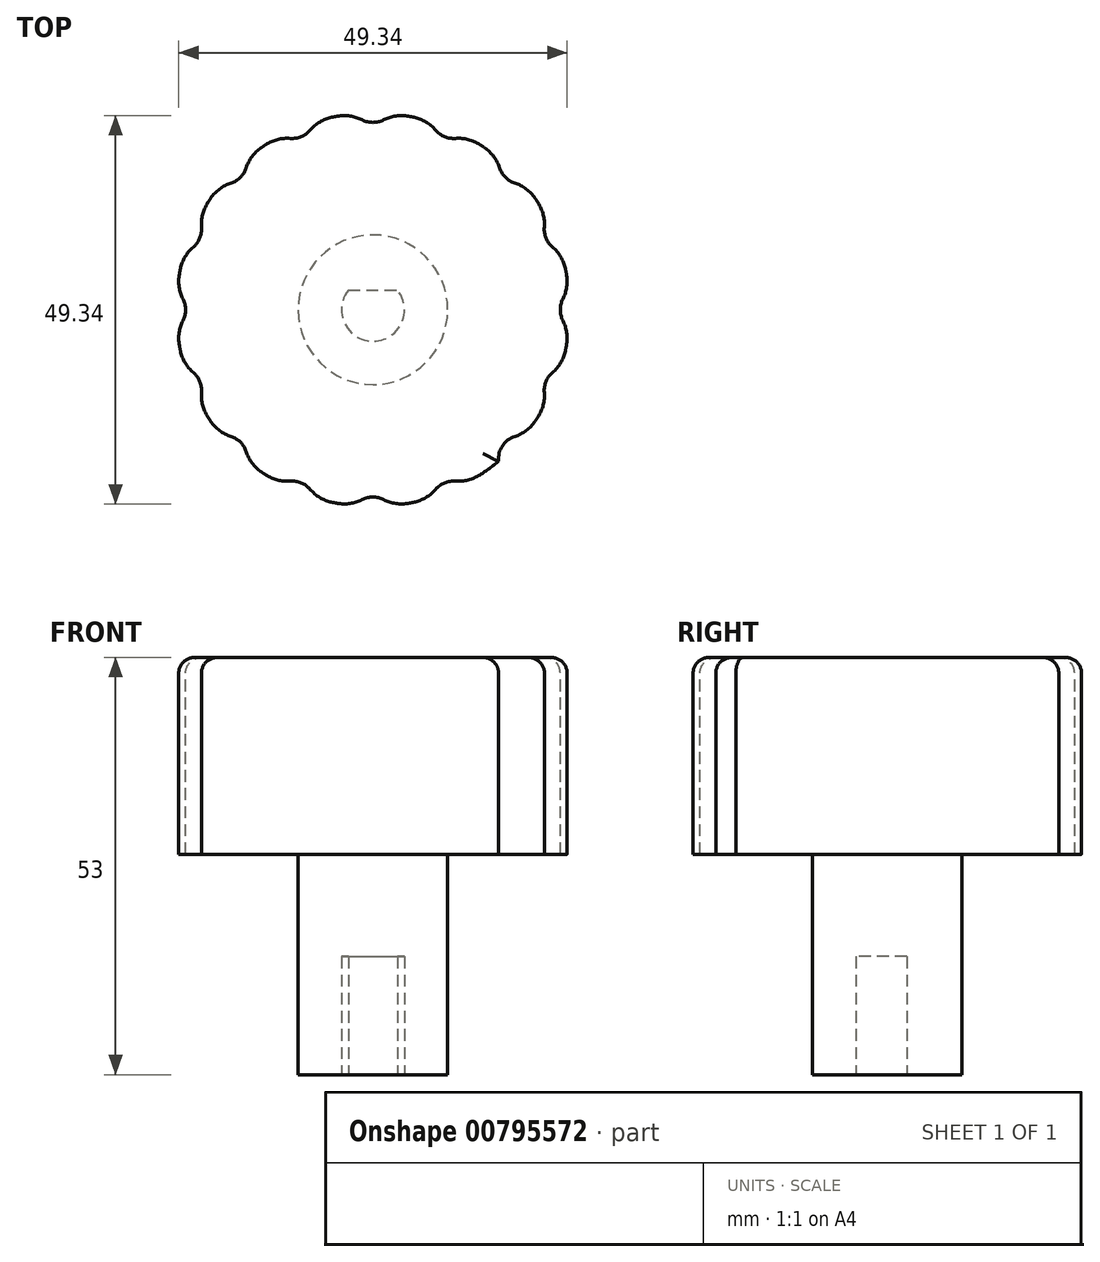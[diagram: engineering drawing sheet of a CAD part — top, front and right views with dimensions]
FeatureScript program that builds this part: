
annotation { "Feature Type Name" : "Feature", "Feature Type Description" : "" }
export const myFeature = defineFeature(function(context is Context, id is Id, definition is map)
    precondition{}
    {
        {
            var Q0;
            Q0=qCreatedBy(makeId("Top.planeOp"),FACE);
            cPlane(context, id + "F0", {"entities" : qUnion([Q0]), "cplaneType" : CPlaneType.OFFSET, "offset" : 25 * mm, "oppositeDirection" : true, "width" : 152.4 * mm, "height" : 152.4 * mm});
        }
        {
            var Q0;
            Q0=qCreatedBy(id+"F0.planeOp",FACE);
            cPlane(context, id + "F1", {"entities" : qUnion([Q0]), "cplaneType" : CPlaneType.OFFSET, "offset" : 1 * mm, "oppositeDirection" : true, "width" : 150 * mm, "height" : 150 * mm});
        }
        {
            var Q0;
            Q0=qCreatedBy(id+"F1.planeOp",FACE);
            cPlane(context, id + "F2", {"entities" : qUnion([Q0]), "cplaneType" : CPlaneType.OFFSET, "offset" : 27 * mm, "oppositeDirection" : true, "width" : 150 * mm, "height" : 150 * mm});
        }
        {
            var Q0;
            Q0=qCreatedBy(makeId("Top.planeOp"),FACE);
            var sketch = newSketch(context, id + "F3", { "sketchPlane" : qUnion([Q0])});
            skCircle(sketch, "E0", {"center": v(0, 0) * mm, "radius": 25 * mm});
            skSolve(sketch);
        }
        {
            var Q0;
            Q0=makeQuery(id+"F3.imprint","IMPRINT",FACE,{"disambiguationData":[TD([[makeQuery(id+"F3.imprint","IMPRINT",EDGE,{"derivedFrom":sQuery(id+"F3.wireOp",EDGE,"E0")}),1.0]])]});
            var Q1;
            Q1=qCreatedBy(id+"F0.planeOp",FACE);
            extrude(context, id + "F4", {"entities" : qUnion([Q0]), "endBound" : BoundingType.UP_TO_SURFACE, "oppositeDirection" : true, "depth" : 25 * mm, "endBoundEntityFace" : qUnion([Q1]), "offsetDistance" : 25 * mm});
        }
        {
            var Q0;
            Q0=qCreatedBy(id+"F0.planeOp",FACE);
            var sketch = newSketch(context, id + "F5", { "sketchPlane" : qUnion([Q0])});
            skCircle(sketch, "E1", {"center": v(0, 0) * mm, "radius": 9.5 * mm});
            skSolve(sketch);
        }
        {
            var Q0;
            Q0 = qSketchRegion(id + "F5", true);
            var Q1;
            Q1=qCreatedBy(id+"F2.planeOp",FACE);
            extrude(context, id + "F6", {"entities" : qUnion([Q0]), "operationType" : NewBodyOperationType.ADD, "endBound" : BoundingType.UP_TO_SURFACE, "oppositeDirection" : true, "depth" : 25 * mm, "endBoundEntityFace" : qUnion([Q1]), "offsetDistance" : 25 * mm});
        }
        {
            var Q0;
            Q0=qCreatedBy(id+"F2.planeOp",FACE);
            var sketch = newSketch(context, id + "F7", { "sketchPlane" : qUnion([Q0])});
            skArc(sketch, "E2", {"start": v(-3.12, 2.5) * mm, "mid": v(0, -4) * mm, "end": v(3.12, 2.5) * mm});
            skLineSegment(sketch, "E3", {"start": v(-3.12, 2.5) * mm, "end": v(3.12, 2.5) * mm});
            skSolve(sketch);
        }
        {
            var Q0;
            Q0=makeQuery(id+"F7.imprint","IMPRINT",FACE,{"disambiguationData":[TD([[makeQuery(id+"F7.imprint","IMPRINT",EDGE,{"derivedFrom":sQuery(id+"F7.wireOp",EDGE,"E2")}),1.0]])]});
            extrude(context, id + "F8", {"entities" : qUnion([Q0]), "operationType" : NewBodyOperationType.REMOVE, "depth" : 15 * mm, "offsetDistance" : 25 * mm});
        }
        {
            var Q0;
            Q0=qCreatedBy(makeId("Top.planeOp"),FACE);
            var sketch = newSketch(context, id + "F9", { "sketchPlane" : qUnion([Q0])});
            skCircle(sketch, "E4", {"center": v(0, 26.8) * mm, "radius": 3 * mm});
            skSolve(sketch);
        }
        {
            var Q0;
            Q0=makeQuery(id+"F9.imprint","IMPRINT",FACE,{"disambiguationData":[TD([[makeQuery(id+"F9.imprint","IMPRINT",EDGE,{"derivedFrom":sQuery(id+"F9.wireOp",EDGE,"E4")}),1.0]])]});
            var Q1;
            Q1=makeQuery(id+"F4.opExtrude","CAP_FACE",FACE,{"disambiguationData":[OSD([sQuery(id+"F3.wireOp",EDGE,"E0")])],"isStart":false});
            extrude(context, id + "F10", {"entities" : qUnion([Q0]), "endBound" : BoundingType.UP_TO_SURFACE, "oppositeDirection" : true, "depth" : 25 * mm, "endBoundEntityFace" : qUnion([Q1]), "offsetDistance" : 25 * mm});
        }
        {
            var Q0;
            Q0=makeQuery(id+"F10.opExtrude","SWEPT_BODY",BODY,{"disambiguationData":[OSD([sQuery(id+"F9.wireOp",EDGE,"E4")])]});
            var Q1;
            Q1=makeQuery(id+"F4.opExtrude","CAP_EDGE",EDGE,{"disambiguationData":[OSD([sQuery(id+"F3.wireOp",EDGE,"E0")])],"isStart":true});
            circularPattern(context, id + "F11", {"entities" : qUnion([Q0]), "axis" : qUnion([Q1]), "angle" : 360 * degree, "instanceCount" : 16, "equalSpace" : true});
        }
        {
            var Q0;
            Q0=makeQuery(id+"F10.opExtrude","SWEPT_BODY",BODY,{"disambiguationData":[OSD([sQuery(id+"F9.wireOp",EDGE,"E4")])]});
            var Q1;
            Q1=makeQuery(id+"F11.opPattern","COPY",BODY,{"derivedFrom":makeQuery(id+"F10.opExtrude","SWEPT_BODY",BODY,{"disambiguationData":[OSD([sQuery(id+"F9.wireOp",EDGE,"E4")])]}),"instanceName":"1"});
            var Q2;
            Q2=makeQuery(id+"F11.opPattern","COPY",BODY,{"derivedFrom":makeQuery(id+"F10.opExtrude","SWEPT_BODY",BODY,{"disambiguationData":[OSD([sQuery(id+"F9.wireOp",EDGE,"E4")])]}),"instanceName":"2"});
            var Q3;
            Q3=makeQuery(id+"F11.opPattern","COPY",BODY,{"derivedFrom":makeQuery(id+"F10.opExtrude","SWEPT_BODY",BODY,{"disambiguationData":[OSD([sQuery(id+"F9.wireOp",EDGE,"E4")])]}),"instanceName":"3"});
            var Q4;
            Q4=makeQuery(id+"F11.opPattern","COPY",BODY,{"derivedFrom":makeQuery(id+"F10.opExtrude","SWEPT_BODY",BODY,{"disambiguationData":[OSD([sQuery(id+"F9.wireOp",EDGE,"E4")])]}),"instanceName":"4"});
            var Q5;
            Q5=makeQuery(id+"F11.opPattern","COPY",BODY,{"derivedFrom":makeQuery(id+"F10.opExtrude","SWEPT_BODY",BODY,{"disambiguationData":[OSD([sQuery(id+"F9.wireOp",EDGE,"E4")])]}),"instanceName":"5"});
            var Q6;
            Q6=makeQuery(id+"F11.opPattern","COPY",BODY,{"derivedFrom":makeQuery(id+"F10.opExtrude","SWEPT_BODY",BODY,{"disambiguationData":[OSD([sQuery(id+"F9.wireOp",EDGE,"E4")])]}),"instanceName":"6"});
            var Q7;
            Q7=makeQuery(id+"F11.opPattern","COPY",BODY,{"derivedFrom":makeQuery(id+"F10.opExtrude","SWEPT_BODY",BODY,{"disambiguationData":[OSD([sQuery(id+"F9.wireOp",EDGE,"E4")])]}),"instanceName":"7"});
            var Q8;
            Q8=makeQuery(id+"F11.opPattern","COPY",BODY,{"derivedFrom":makeQuery(id+"F10.opExtrude","SWEPT_BODY",BODY,{"disambiguationData":[OSD([sQuery(id+"F9.wireOp",EDGE,"E4")])]}),"instanceName":"8"});
            var Q9;
            Q9=makeQuery(id+"F11.opPattern","COPY",BODY,{"derivedFrom":makeQuery(id+"F10.opExtrude","SWEPT_BODY",BODY,{"disambiguationData":[OSD([sQuery(id+"F9.wireOp",EDGE,"E4")])]}),"instanceName":"9"});
            var Q10;
            Q10=makeQuery(id+"F11.opPattern","COPY",BODY,{"derivedFrom":makeQuery(id+"F10.opExtrude","SWEPT_BODY",BODY,{"disambiguationData":[OSD([sQuery(id+"F9.wireOp",EDGE,"E4")])]}),"instanceName":"10"});
            var Q11;
            Q11=makeQuery(id+"F11.opPattern","COPY",BODY,{"derivedFrom":makeQuery(id+"F10.opExtrude","SWEPT_BODY",BODY,{"disambiguationData":[OSD([sQuery(id+"F9.wireOp",EDGE,"E4")])]}),"instanceName":"11"});
            var Q12;
            Q12=makeQuery(id+"F11.opPattern","COPY",BODY,{"derivedFrom":makeQuery(id+"F10.opExtrude","SWEPT_BODY",BODY,{"disambiguationData":[OSD([sQuery(id+"F9.wireOp",EDGE,"E4")])]}),"instanceName":"12"});
            var Q13;
            Q13=makeQuery(id+"F11.opPattern","COPY",BODY,{"derivedFrom":makeQuery(id+"F10.opExtrude","SWEPT_BODY",BODY,{"disambiguationData":[OSD([sQuery(id+"F9.wireOp",EDGE,"E4")])]}),"instanceName":"13"});
            var Q14;
            Q14=makeQuery(id+"F11.opPattern","COPY",BODY,{"derivedFrom":makeQuery(id+"F10.opExtrude","SWEPT_BODY",BODY,{"disambiguationData":[OSD([sQuery(id+"F9.wireOp",EDGE,"E4")])]}),"instanceName":"14"});
            var Q15;
            Q15=makeQuery(id+"F11.opPattern","COPY",BODY,{"derivedFrom":makeQuery(id+"F10.opExtrude","SWEPT_BODY",BODY,{"disambiguationData":[OSD([sQuery(id+"F9.wireOp",EDGE,"E4")])]}),"instanceName":"15"});
            var Q16;
            Q16=makeQuery(id+"F4.opExtrude","SWEPT_BODY",BODY,{"disambiguationData":[OSD([sQuery(id+"F3.wireOp",EDGE,"E0")])]});
            booleanBodies(context, id + "F12", {"operationType" : BooleanOperationType.SUBTRACTION, "tools" : qUnion([Q0, Q1, Q2, Q3, Q4, Q5, Q6, Q7, Q8, Q9, Q10, Q11, Q12, Q13, Q14, Q15]), "targets" : qUnion([Q16])});
        }
        {
            var Q0;
            Q0=makeQuery(id+"F12.opBoolean","INTERSECT",EDGE,{"disambiguationData":[OD(0.0)],"derivedFrom":[makeQuery(id+"F4.opExtrude","SWEPT_FACE",FACE,{"disambiguationData":[OSD([sQuery(id+"F3.wireOp",EDGE,"E0")])]}),makeQuery(id+"F10.opExtrude","SWEPT_FACE",FACE,{"disambiguationData":[OSD([sQuery(id+"F9.wireOp",EDGE,"E4")])]})]});
            var Q1;
            Q1=makeQuery(id+"F12.opBoolean","INTERSECT",EDGE,{"disambiguationData":[OD(1.0)],"derivedFrom":[makeQuery(id+"F4.opExtrude","SWEPT_FACE",FACE,{"disambiguationData":[OSD([sQuery(id+"F3.wireOp",EDGE,"E0")])]}),makeQuery(id+"F10.opExtrude","SWEPT_FACE",FACE,{"disambiguationData":[OSD([sQuery(id+"F9.wireOp",EDGE,"E4")])]})]});
            var Q2;
            Q2=makeQuery(id+"F12.opBoolean","INTERSECT",EDGE,{"disambiguationData":[OD(0.0)],"derivedFrom":[makeQuery(id+"F4.opExtrude","SWEPT_FACE",FACE,{"disambiguationData":[OSD([sQuery(id+"F3.wireOp",EDGE,"E0")])]}),makeQuery(id+"F11.opPattern","COPY",FACE,{"derivedFrom":makeQuery(id+"F10.opExtrude","SWEPT_FACE",FACE,{"disambiguationData":[OSD([sQuery(id+"F9.wireOp",EDGE,"E4")])]}),"instanceName":"15"})]});
            var Q3;
            Q3=makeQuery(id+"F12.opBoolean","INTERSECT",EDGE,{"disambiguationData":[OD(1.0)],"derivedFrom":[makeQuery(id+"F4.opExtrude","SWEPT_FACE",FACE,{"disambiguationData":[OSD([sQuery(id+"F3.wireOp",EDGE,"E0")])]}),makeQuery(id+"F11.opPattern","COPY",FACE,{"derivedFrom":makeQuery(id+"F10.opExtrude","SWEPT_FACE",FACE,{"disambiguationData":[OSD([sQuery(id+"F9.wireOp",EDGE,"E4")])]}),"instanceName":"15"})]});
            var Q4;
            Q4=makeQuery(id+"F12.opBoolean","INTERSECT",EDGE,{"disambiguationData":[OD(1.0)],"derivedFrom":[makeQuery(id+"F4.opExtrude","SWEPT_FACE",FACE,{"disambiguationData":[OSD([sQuery(id+"F3.wireOp",EDGE,"E0")])]}),makeQuery(id+"F11.opPattern","COPY",FACE,{"derivedFrom":makeQuery(id+"F10.opExtrude","SWEPT_FACE",FACE,{"disambiguationData":[OSD([sQuery(id+"F9.wireOp",EDGE,"E4")])]}),"instanceName":"14"})]});
            var Q5;
            Q5=makeQuery(id+"F12.opBoolean","INTERSECT",EDGE,{"disambiguationData":[OD(0.0)],"derivedFrom":[makeQuery(id+"F4.opExtrude","SWEPT_FACE",FACE,{"disambiguationData":[OSD([sQuery(id+"F3.wireOp",EDGE,"E0")])]}),makeQuery(id+"F11.opPattern","COPY",FACE,{"derivedFrom":makeQuery(id+"F10.opExtrude","SWEPT_FACE",FACE,{"disambiguationData":[OSD([sQuery(id+"F9.wireOp",EDGE,"E4")])]}),"instanceName":"14"})]});
            var Q6;
            Q6=makeQuery(id+"F12.opBoolean","INTERSECT",EDGE,{"disambiguationData":[OD(1.0)],"derivedFrom":[makeQuery(id+"F4.opExtrude","SWEPT_FACE",FACE,{"disambiguationData":[OSD([sQuery(id+"F3.wireOp",EDGE,"E0")])]}),makeQuery(id+"F11.opPattern","COPY",FACE,{"derivedFrom":makeQuery(id+"F10.opExtrude","SWEPT_FACE",FACE,{"disambiguationData":[OSD([sQuery(id+"F9.wireOp",EDGE,"E4")])]}),"instanceName":"13"})]});
            var Q7;
            Q7=makeQuery(id+"F12.opBoolean","INTERSECT",EDGE,{"disambiguationData":[OD(0.0)],"derivedFrom":[makeQuery(id+"F4.opExtrude","SWEPT_FACE",FACE,{"disambiguationData":[OSD([sQuery(id+"F3.wireOp",EDGE,"E0")])]}),makeQuery(id+"F11.opPattern","COPY",FACE,{"derivedFrom":makeQuery(id+"F10.opExtrude","SWEPT_FACE",FACE,{"disambiguationData":[OSD([sQuery(id+"F9.wireOp",EDGE,"E4")])]}),"instanceName":"13"})]});
            var Q8;
            Q8=makeQuery(id+"F12.opBoolean","INTERSECT",EDGE,{"disambiguationData":[OD(1.0)],"derivedFrom":[makeQuery(id+"F4.opExtrude","SWEPT_FACE",FACE,{"disambiguationData":[OSD([sQuery(id+"F3.wireOp",EDGE,"E0")])]}),makeQuery(id+"F11.opPattern","COPY",FACE,{"derivedFrom":makeQuery(id+"F10.opExtrude","SWEPT_FACE",FACE,{"disambiguationData":[OSD([sQuery(id+"F9.wireOp",EDGE,"E4")])]}),"instanceName":"12"})]});
            var Q9;
            Q9=makeQuery(id+"F12.opBoolean","INTERSECT",EDGE,{"disambiguationData":[OD(0.0)],"derivedFrom":[makeQuery(id+"F4.opExtrude","SWEPT_FACE",FACE,{"disambiguationData":[OSD([sQuery(id+"F3.wireOp",EDGE,"E0")])]}),makeQuery(id+"F11.opPattern","COPY",FACE,{"derivedFrom":makeQuery(id+"F10.opExtrude","SWEPT_FACE",FACE,{"disambiguationData":[OSD([sQuery(id+"F9.wireOp",EDGE,"E4")])]}),"instanceName":"12"})]});
            var Q10;
            Q10=makeQuery(id+"F12.opBoolean","INTERSECT",EDGE,{"disambiguationData":[OD(1.0)],"derivedFrom":[makeQuery(id+"F4.opExtrude","SWEPT_FACE",FACE,{"disambiguationData":[OSD([sQuery(id+"F3.wireOp",EDGE,"E0")])]}),makeQuery(id+"F11.opPattern","COPY",FACE,{"derivedFrom":makeQuery(id+"F10.opExtrude","SWEPT_FACE",FACE,{"disambiguationData":[OSD([sQuery(id+"F9.wireOp",EDGE,"E4")])]}),"instanceName":"11"})]});
            var Q11;
            Q11=makeQuery(id+"F12.opBoolean","INTERSECT",EDGE,{"disambiguationData":[OD(0.0)],"derivedFrom":[makeQuery(id+"F4.opExtrude","SWEPT_FACE",FACE,{"disambiguationData":[OSD([sQuery(id+"F3.wireOp",EDGE,"E0")])]}),makeQuery(id+"F11.opPattern","COPY",FACE,{"derivedFrom":makeQuery(id+"F10.opExtrude","SWEPT_FACE",FACE,{"disambiguationData":[OSD([sQuery(id+"F9.wireOp",EDGE,"E4")])]}),"instanceName":"11"})]});
            var Q12;
            Q12=makeQuery(id+"F12.opBoolean","INTERSECT",EDGE,{"disambiguationData":[OD(1.0)],"derivedFrom":[makeQuery(id+"F4.opExtrude","SWEPT_FACE",FACE,{"disambiguationData":[OSD([sQuery(id+"F3.wireOp",EDGE,"E0")])]}),makeQuery(id+"F11.opPattern","COPY",FACE,{"derivedFrom":makeQuery(id+"F10.opExtrude","SWEPT_FACE",FACE,{"disambiguationData":[OSD([sQuery(id+"F9.wireOp",EDGE,"E4")])]}),"instanceName":"10"})]});
            var Q13;
            Q13=makeQuery(id+"F12.opBoolean","INTERSECT",EDGE,{"disambiguationData":[OD(1.0)],"derivedFrom":[makeQuery(id+"F4.opExtrude","SWEPT_FACE",FACE,{"disambiguationData":[OSD([sQuery(id+"F3.wireOp",EDGE,"E0")])]}),makeQuery(id+"F11.opPattern","COPY",FACE,{"derivedFrom":makeQuery(id+"F10.opExtrude","SWEPT_FACE",FACE,{"disambiguationData":[OSD([sQuery(id+"F9.wireOp",EDGE,"E4")])]}),"instanceName":"9"})]});
            var Q14;
            Q14=makeQuery(id+"F12.opBoolean","INTERSECT",EDGE,{"disambiguationData":[OD(0.0)],"derivedFrom":[makeQuery(id+"F4.opExtrude","SWEPT_FACE",FACE,{"disambiguationData":[OSD([sQuery(id+"F3.wireOp",EDGE,"E0")])]}),makeQuery(id+"F11.opPattern","COPY",FACE,{"derivedFrom":makeQuery(id+"F10.opExtrude","SWEPT_FACE",FACE,{"disambiguationData":[OSD([sQuery(id+"F9.wireOp",EDGE,"E4")])]}),"instanceName":"9"})]});
            var Q15;
            Q15=makeQuery(id+"F12.opBoolean","INTERSECT",EDGE,{"disambiguationData":[OD(1.0)],"derivedFrom":[makeQuery(id+"F4.opExtrude","SWEPT_FACE",FACE,{"disambiguationData":[OSD([sQuery(id+"F3.wireOp",EDGE,"E0")])]}),makeQuery(id+"F11.opPattern","COPY",FACE,{"derivedFrom":makeQuery(id+"F10.opExtrude","SWEPT_FACE",FACE,{"disambiguationData":[OSD([sQuery(id+"F9.wireOp",EDGE,"E4")])]}),"instanceName":"8"})]});
            var Q16;
            Q16=makeQuery(id+"F12.opBoolean","INTERSECT",EDGE,{"disambiguationData":[OD(0.0)],"derivedFrom":[makeQuery(id+"F4.opExtrude","SWEPT_FACE",FACE,{"disambiguationData":[OSD([sQuery(id+"F3.wireOp",EDGE,"E0")])]}),makeQuery(id+"F11.opPattern","COPY",FACE,{"derivedFrom":makeQuery(id+"F10.opExtrude","SWEPT_FACE",FACE,{"disambiguationData":[OSD([sQuery(id+"F9.wireOp",EDGE,"E4")])]}),"instanceName":"8"})]});
            var Q17;
            Q17=makeQuery(id+"F12.opBoolean","INTERSECT",EDGE,{"disambiguationData":[OD(1.0)],"derivedFrom":[makeQuery(id+"F4.opExtrude","SWEPT_FACE",FACE,{"disambiguationData":[OSD([sQuery(id+"F3.wireOp",EDGE,"E0")])]}),makeQuery(id+"F11.opPattern","COPY",FACE,{"derivedFrom":makeQuery(id+"F10.opExtrude","SWEPT_FACE",FACE,{"disambiguationData":[OSD([sQuery(id+"F9.wireOp",EDGE,"E4")])]}),"instanceName":"7"})]});
            var Q18;
            Q18=makeQuery(id+"F12.opBoolean","INTERSECT",EDGE,{"disambiguationData":[OD(0.0)],"derivedFrom":[makeQuery(id+"F4.opExtrude","SWEPT_FACE",FACE,{"disambiguationData":[OSD([sQuery(id+"F3.wireOp",EDGE,"E0")])]}),makeQuery(id+"F11.opPattern","COPY",FACE,{"derivedFrom":makeQuery(id+"F10.opExtrude","SWEPT_FACE",FACE,{"disambiguationData":[OSD([sQuery(id+"F9.wireOp",EDGE,"E4")])]}),"instanceName":"7"})]});
            var Q19;
            Q19=makeQuery(id+"F12.opBoolean","INTERSECT",EDGE,{"disambiguationData":[OD(1.0)],"derivedFrom":[makeQuery(id+"F4.opExtrude","SWEPT_FACE",FACE,{"disambiguationData":[OSD([sQuery(id+"F3.wireOp",EDGE,"E0")])]}),makeQuery(id+"F11.opPattern","COPY",FACE,{"derivedFrom":makeQuery(id+"F10.opExtrude","SWEPT_FACE",FACE,{"disambiguationData":[OSD([sQuery(id+"F9.wireOp",EDGE,"E4")])]}),"instanceName":"6"})]});
            var Q20;
            Q20=makeQuery(id+"F12.opBoolean","INTERSECT",EDGE,{"disambiguationData":[OD(0.0)],"derivedFrom":[makeQuery(id+"F4.opExtrude","SWEPT_FACE",FACE,{"disambiguationData":[OSD([sQuery(id+"F3.wireOp",EDGE,"E0")])]}),makeQuery(id+"F11.opPattern","COPY",FACE,{"derivedFrom":makeQuery(id+"F10.opExtrude","SWEPT_FACE",FACE,{"disambiguationData":[OSD([sQuery(id+"F9.wireOp",EDGE,"E4")])]}),"instanceName":"6"})]});
            var Q21;
            Q21=makeQuery(id+"F12.opBoolean","INTERSECT",EDGE,{"disambiguationData":[OD(1.0)],"derivedFrom":[makeQuery(id+"F4.opExtrude","SWEPT_FACE",FACE,{"disambiguationData":[OSD([sQuery(id+"F3.wireOp",EDGE,"E0")])]}),makeQuery(id+"F11.opPattern","COPY",FACE,{"derivedFrom":makeQuery(id+"F10.opExtrude","SWEPT_FACE",FACE,{"disambiguationData":[OSD([sQuery(id+"F9.wireOp",EDGE,"E4")])]}),"instanceName":"5"})]});
            var Q22;
            Q22=makeQuery(id+"F12.opBoolean","INTERSECT",EDGE,{"disambiguationData":[OD(0.0)],"derivedFrom":[makeQuery(id+"F4.opExtrude","SWEPT_FACE",FACE,{"disambiguationData":[OSD([sQuery(id+"F3.wireOp",EDGE,"E0")])]}),makeQuery(id+"F11.opPattern","COPY",FACE,{"derivedFrom":makeQuery(id+"F10.opExtrude","SWEPT_FACE",FACE,{"disambiguationData":[OSD([sQuery(id+"F9.wireOp",EDGE,"E4")])]}),"instanceName":"5"})]});
            var Q23;
            Q23=makeQuery(id+"F12.opBoolean","INTERSECT",EDGE,{"disambiguationData":[OD(1.0)],"derivedFrom":[makeQuery(id+"F4.opExtrude","SWEPT_FACE",FACE,{"disambiguationData":[OSD([sQuery(id+"F3.wireOp",EDGE,"E0")])]}),makeQuery(id+"F11.opPattern","COPY",FACE,{"derivedFrom":makeQuery(id+"F10.opExtrude","SWEPT_FACE",FACE,{"disambiguationData":[OSD([sQuery(id+"F9.wireOp",EDGE,"E4")])]}),"instanceName":"4"})]});
            var Q24;
            Q24=makeQuery(id+"F12.opBoolean","INTERSECT",EDGE,{"disambiguationData":[OD(0.0)],"derivedFrom":[makeQuery(id+"F4.opExtrude","SWEPT_FACE",FACE,{"disambiguationData":[OSD([sQuery(id+"F3.wireOp",EDGE,"E0")])]}),makeQuery(id+"F11.opPattern","COPY",FACE,{"derivedFrom":makeQuery(id+"F10.opExtrude","SWEPT_FACE",FACE,{"disambiguationData":[OSD([sQuery(id+"F9.wireOp",EDGE,"E4")])]}),"instanceName":"4"})]});
            var Q25;
            Q25=makeQuery(id+"F12.opBoolean","INTERSECT",EDGE,{"disambiguationData":[OD(1.0)],"derivedFrom":[makeQuery(id+"F4.opExtrude","SWEPT_FACE",FACE,{"disambiguationData":[OSD([sQuery(id+"F3.wireOp",EDGE,"E0")])]}),makeQuery(id+"F11.opPattern","COPY",FACE,{"derivedFrom":makeQuery(id+"F10.opExtrude","SWEPT_FACE",FACE,{"disambiguationData":[OSD([sQuery(id+"F9.wireOp",EDGE,"E4")])]}),"instanceName":"3"})]});
            var Q26;
            Q26=makeQuery(id+"F12.opBoolean","INTERSECT",EDGE,{"disambiguationData":[OD(0.0)],"derivedFrom":[makeQuery(id+"F4.opExtrude","SWEPT_FACE",FACE,{"disambiguationData":[OSD([sQuery(id+"F3.wireOp",EDGE,"E0")])]}),makeQuery(id+"F11.opPattern","COPY",FACE,{"derivedFrom":makeQuery(id+"F10.opExtrude","SWEPT_FACE",FACE,{"disambiguationData":[OSD([sQuery(id+"F9.wireOp",EDGE,"E4")])]}),"instanceName":"3"})]});
            var Q27;
            Q27=makeQuery(id+"F12.opBoolean","INTERSECT",EDGE,{"disambiguationData":[OD(1.0)],"derivedFrom":[makeQuery(id+"F4.opExtrude","SWEPT_FACE",FACE,{"disambiguationData":[OSD([sQuery(id+"F3.wireOp",EDGE,"E0")])]}),makeQuery(id+"F11.opPattern","COPY",FACE,{"derivedFrom":makeQuery(id+"F10.opExtrude","SWEPT_FACE",FACE,{"disambiguationData":[OSD([sQuery(id+"F9.wireOp",EDGE,"E4")])]}),"instanceName":"2"})]});
            var Q28;
            Q28=makeQuery(id+"F12.opBoolean","INTERSECT",EDGE,{"disambiguationData":[OD(0.0)],"derivedFrom":[makeQuery(id+"F4.opExtrude","SWEPT_FACE",FACE,{"disambiguationData":[OSD([sQuery(id+"F3.wireOp",EDGE,"E0")])]}),makeQuery(id+"F11.opPattern","COPY",FACE,{"derivedFrom":makeQuery(id+"F10.opExtrude","SWEPT_FACE",FACE,{"disambiguationData":[OSD([sQuery(id+"F9.wireOp",EDGE,"E4")])]}),"instanceName":"2"})]});
            var Q29;
            Q29=makeQuery(id+"F12.opBoolean","INTERSECT",EDGE,{"disambiguationData":[OD(1.0)],"derivedFrom":[makeQuery(id+"F4.opExtrude","SWEPT_FACE",FACE,{"disambiguationData":[OSD([sQuery(id+"F3.wireOp",EDGE,"E0")])]}),makeQuery(id+"F11.opPattern","COPY",FACE,{"derivedFrom":makeQuery(id+"F10.opExtrude","SWEPT_FACE",FACE,{"disambiguationData":[OSD([sQuery(id+"F9.wireOp",EDGE,"E4")])]}),"instanceName":"1"})]});
            var Q30;
            Q30=makeQuery(id+"F12.opBoolean","INTERSECT",EDGE,{"disambiguationData":[OD(0.0)],"derivedFrom":[makeQuery(id+"F4.opExtrude","SWEPT_FACE",FACE,{"disambiguationData":[OSD([sQuery(id+"F3.wireOp",EDGE,"E0")])]}),makeQuery(id+"F11.opPattern","COPY",FACE,{"derivedFrom":makeQuery(id+"F10.opExtrude","SWEPT_FACE",FACE,{"disambiguationData":[OSD([sQuery(id+"F9.wireOp",EDGE,"E4")])]}),"instanceName":"1"})]});
            fillet(context, id + "F13", {"entities" : qUnion([Q0, Q1, Q2, Q3, Q4, Q5, Q6, Q7, Q8, Q9, Q10, Q11, Q12, Q13, Q14, Q15, Q16, Q17, Q18, Q19, Q20, Q21, Q22, Q23, Q24, Q25, Q26, Q27, Q28, Q29, Q30]), "radius" : 5 * mm, "tangentPropagation" : true, "allowEdgeOverflow" : false});
        }
        {
            var Q0;
            {var subQ0=sQuery(id+"F3.wireOp",EDGE,"E0");Q0=makeQuery(id+"F13.opFillet","BLEND_EDGE",EDGE,{"blendedFrom":[makeQuery(id+"F12.opBoolean","INTERSECT",EDGE,{"disambiguationData":[OD(1.0)],"derivedFrom":[makeQuery(id+"F4.opExtrude","SWEPT_FACE",FACE,{"disambiguationData":[OSD([subQ0])]}),makeQuery(id+"F11.opPattern","COPY",FACE,{"derivedFrom":makeQuery(id+"F10.opExtrude","SWEPT_FACE",FACE,{"disambiguationData":[OSD([sQuery(id+"F9.wireOp",EDGE,"E4")])]}),"instanceName":"4"})]}),makeQuery(id+"F4.opExtrude","CAP_FACE",FACE,{"disambiguationData":[OSD([subQ0])],"isStart":true})],"blendedInto":[makeQuery(id+"F4.opExtrude","CAP_FACE",FACE,{"disambiguationData":[OSD([subQ0])],"isStart":true})]});}
            var Q1;
            Q1=makeQuery(id+"F6.opExtrude","CAP_EDGE",EDGE,{"disambiguationData":[OSD([sQuery(id+"F5.wireOp",EDGE,"E1")])],"isStart":true});
            fillet(context, id + "F14", {"entities" : qUnion([Q0, Q1]), "radius" : 2 * mm, "tangentPropagation" : true, "allowEdgeOverflow" : false});
        }
    });
